# Revit family: Ascoli Desk Light (Issue2)
name_source: partatom
category: Lighting Fixtures
revit_build: Autodesk Revit 2018 (Build: 20170223_1515(x64)
units: mm (PartAtom-declared; Revit-internal decimal feet)

## family parameters
Always vertical = Yes
Cut with Voids When Loaded = No
Light Source = No
OmniClass Number = 23.80.70.00
OmniClass Title = Lighting
Part Type = Normal
Room Calculation Point = No
Round Connector Dimension = Use Diameter
Shared = No
Work Plane-Based = No

## types (4) — shared parameters
Dimmable = No
Driver Required = No
Efficacy (lm/W) = Lamp Dependant
Electrical Class = Class 2
Lamp = GU 10 LED
Length of Cable Supplied = 2000 mm
Light Source Fixed = No
Location / IP Rating = IP20
Main Material = Metal - Steel/Zinc/Aluminium
Manufacturer URL - Europe and Rest of World = www.astrolighting.com
Manufacturer URL - North America = us.astrolighting.com
Power (W) = 6 W LED Max
Product CCT = Lamp Dependant
Product CRI = Lamp Dependant
Product Dimensions (MM) = H 420 W 135 D 210
Product Location = Indoors
Product URL = https://www.astrolighting.com
Product Weight (KG) = 1.76
Wattage Comments = -

## per-type parameters (varying)
| type | Main Finish | Product Name | Product SKU |
| Astro Ascoli Desk - Matt White | Matt White | Ascoli Desk | 1286016 |
| Astro Ascoli Desk - Matt Nickel | Matt Nickel | Ascoli Floor | 1286017 |
| Astro Ascoli Desk - Bronze | Bronze | Ascoli Floor | 1286024 |
| Astro Ascoli Desk - Matt Black | Matt Black | Ascoli Desk | 1286086 |

## geometry (parser evidence)
native form markers: Sweep x2
no freeform markers — native parametric forms only
